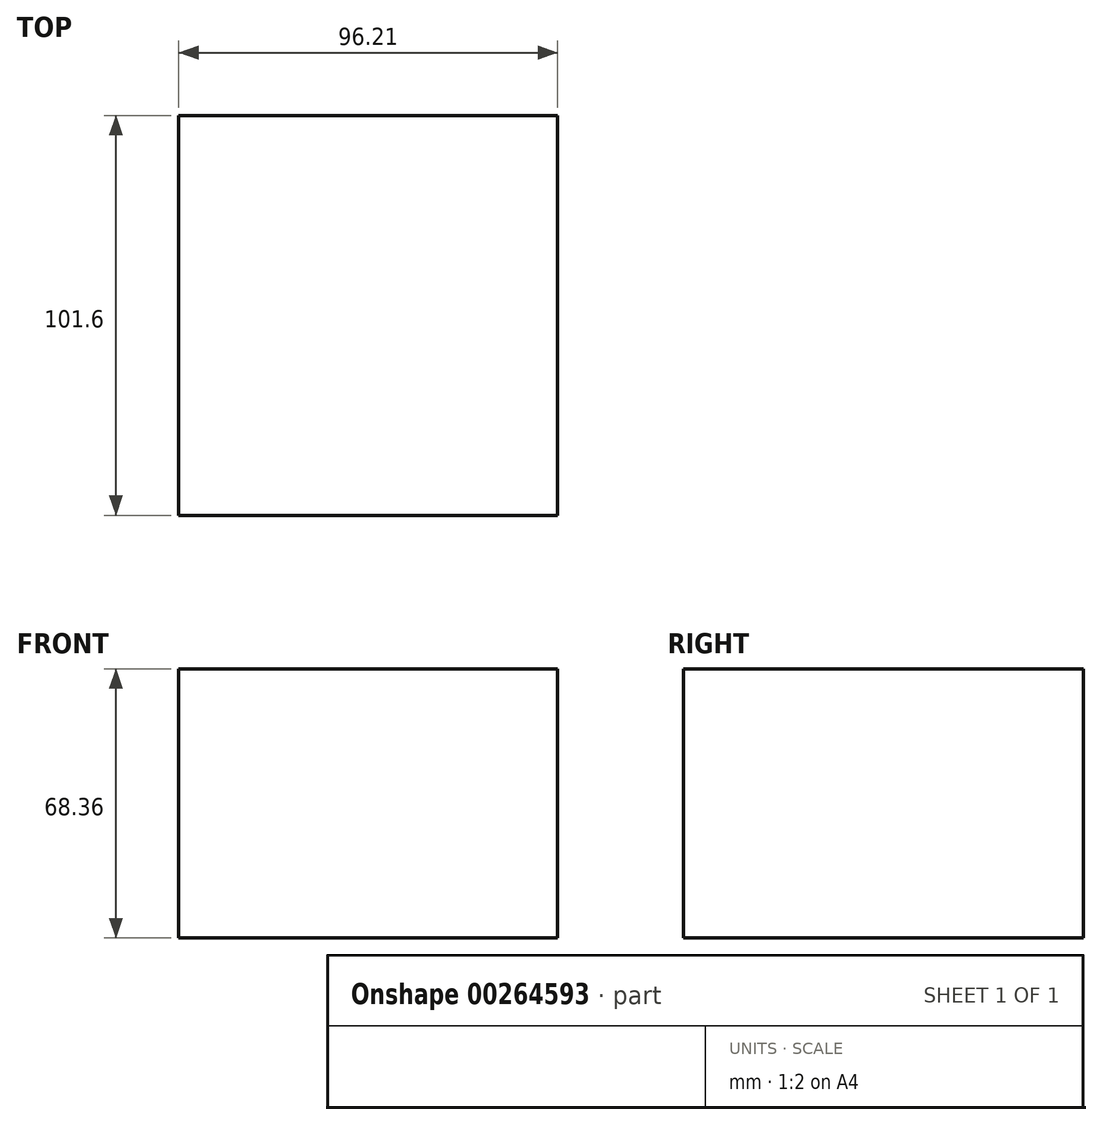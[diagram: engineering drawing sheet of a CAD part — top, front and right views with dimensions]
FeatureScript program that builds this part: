
annotation { "Feature Type Name" : "Feature", "Feature Type Description" : "" }
export const myFeature = defineFeature(function(context is Context, id is Id, definition is map)
    precondition{}
    {
        {
            var Q0;
            Q0=qCreatedBy(makeId("Front.planeOp"),FACE);
            var sketch = newSketch(context, id + "F0", { "sketchPlane" : qUnion([Q0])});
            skLineSegment(sketch, "E0.bottom", {"start": v(0, 0) * mm, "end": v(-96.2, 0) * mm});
            skLineSegment(sketch, "E0.top", {"start": v(0, -68.36) * mm, "end": v(-96.2, -68.36) * mm});
            skLineSegment(sketch, "E0.left", {"start": v(0, 0) * mm, "end": v(0, -68.36) * mm});
            skLineSegment(sketch, "E0.right", {"start": v(-96.2, 0) * mm, "end": v(-96.2, -68.36) * mm});
            skCircle(sketch, "E1", {"center": v(-51.34, -31.99) * mm, "radius": 28.44 * mm});
            skSolve(sketch);
        }
        {
            var Q0;
            Q0 = qSketchRegion(id + "F0", true);
            var Q1;
            Q1=makeQuery(id+"F0.imprint","IMPRINT",FACE,{"disambiguationData":[TD([[makeQuery(id+"F0.imprint","IMPRINT",EDGE,{"derivedFrom":sQuery(id+"F0.wireOp",EDGE,"E1")}),1.0]])]});
            extrude(context, id + "F1", {"entities" : qUnion([Q0, Q1]), "oppositeDirection" : true, "depth" : 101.6 * mm});
        }
    });
